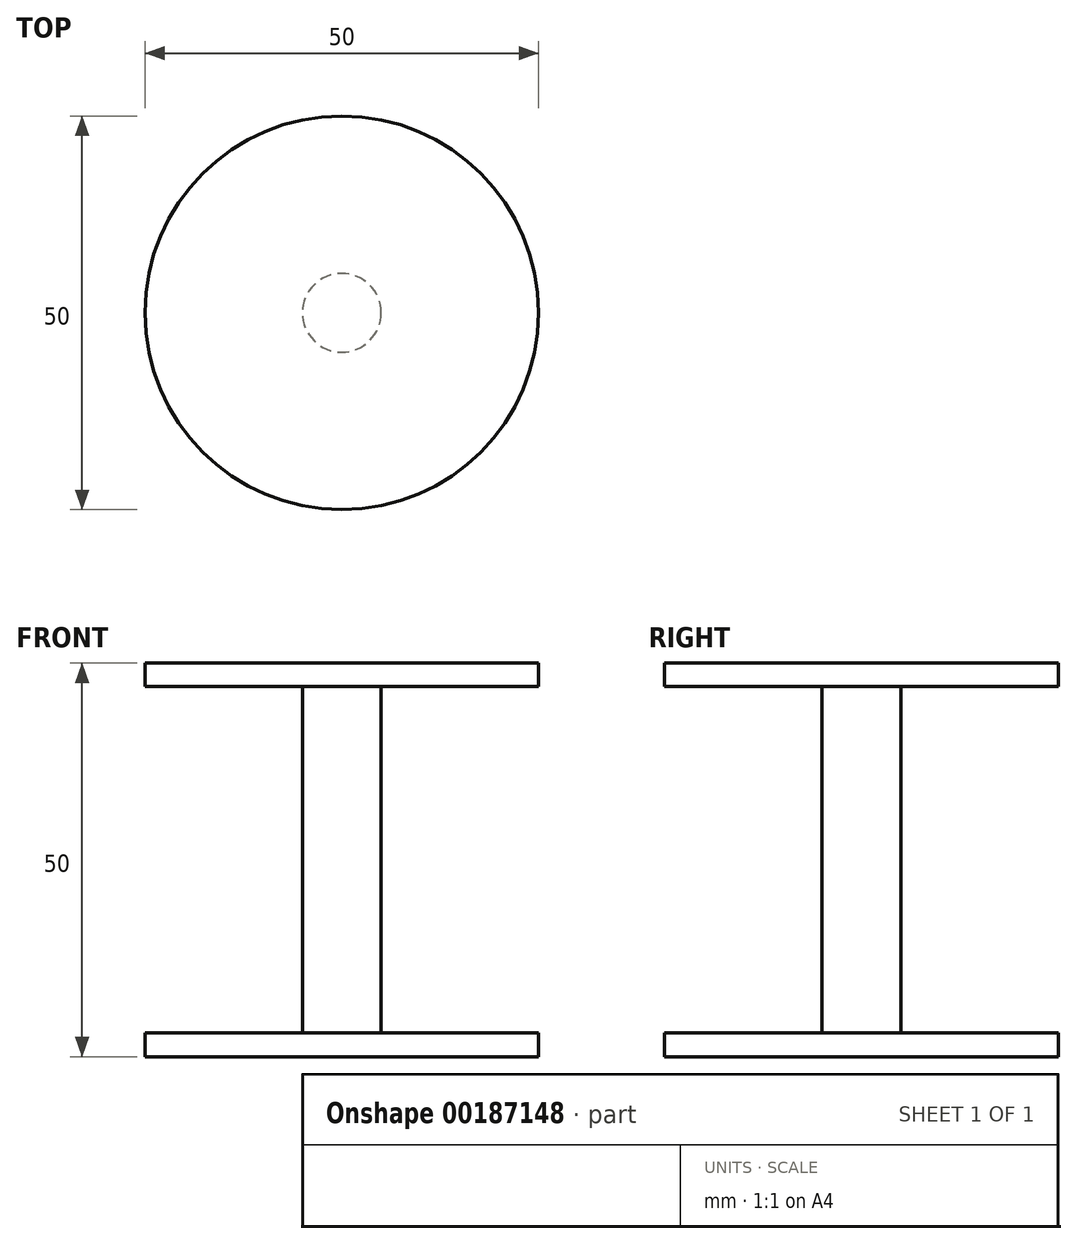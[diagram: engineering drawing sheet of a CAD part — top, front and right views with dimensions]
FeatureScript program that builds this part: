
annotation { "Feature Type Name" : "Feature", "Feature Type Description" : "" }
export const myFeature = defineFeature(function(context is Context, id is Id, definition is map)
    precondition{}
    {
        {
            var Q0;
            Q0=qCreatedBy(makeId("Front.planeOp"),FACE);
            var sketch = newSketch(context, id + "F0", { "sketchPlane" : qUnion([Q0])});
            skLineSegment(sketch, "E0", {"start": v(0, 0) * mm, "end": v(0, 50) * mm});
            skLineSegment(sketch, "E1", {"start": v(0, 50) * mm, "end": v(25, 50) * mm});
            skLineSegment(sketch, "E2", {"start": v(25, 50) * mm, "end": v(25, 47) * mm});
            skLineSegment(sketch, "E3", {"start": v(25, 47) * mm, "end": v(5, 47) * mm});
            skLineSegment(sketch, "E4", {"start": v(5, 47) * mm, "end": v(5, 25) * mm});
            skPoint(sketch, "E4.endSnap0", {"position": v(0, 25) * mm});
            skLineSegment(sketch, "E5", {"start": v(5, 25) * mm, "end": v(10.43, 25) * mm});
            skLineSegment(sketch, "E6.MirrorCS", {"start": v(5, 3) * mm, "end": v(5, 25) * mm});
            skLineSegment(sketch, "E7.MirrorCS", {"start": v(25, 3) * mm, "end": v(5, 3) * mm});
            skLineSegment(sketch, "E8.MirrorCS", {"start": v(0, 0) * mm, "end": v(25, 0) * mm});
            skLineSegment(sketch, "E9.MirrorCS", {"start": v(25, 0) * mm, "end": v(25, 3) * mm});
            skSolve(sketch);
        }
        {
            var Q0;
            Q0=makeQuery(id+"F0.imprint","IMPRINT",FACE,{"disambiguationData":[TD([[makeQuery(id+"F0.imprint","IMPRINT",EDGE,{"derivedFrom":sQuery(id+"F0.wireOp",EDGE,"E0")}),-1.0]])]});
            var Q1;
            Q1=sQuery(id+"F0.wireOp",EDGE,"E0");
            revolve(context, id + "F1", {"entities" : qUnion([Q0]), "axis" : qUnion([Q1]), "revolveType" : RevolveType.FULL});
        }
    });
